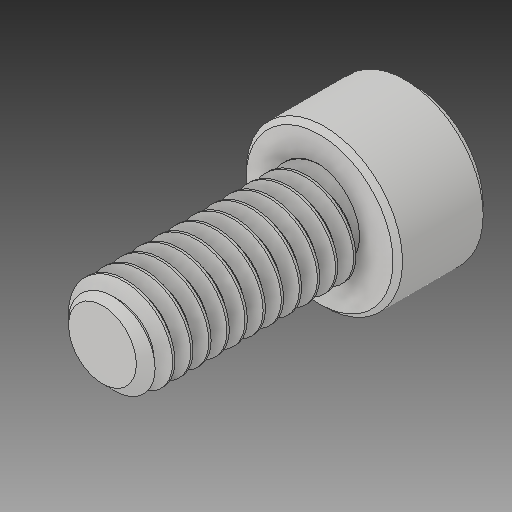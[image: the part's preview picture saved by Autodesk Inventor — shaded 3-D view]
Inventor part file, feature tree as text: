
AUTODESK INVENTOR PART (.ipt)
format: ipt  version: 2018 (Build 220112000, 112)  size: 600,576 bytes
history: native  units: in
note: dims shown in document units (in); Inventor stores cm internally (conversion verified against a paired STEP export)
features: chamfer x1
ambient origin geometry x8: Origin, YZ Plane, XZ Plane, XY Plane, X Axis, Y Axis, Z Axis, Center Point
bodies: Solid1 (feature_tree)
feature tree (1):
  chamfer  "Chamfer2"  [1 undecoded]
note: 1 required parameter value undecoded (feature->parameter linkage not recoverable at this tier; creation-order binding heuristic only, values carry confidence <= 0.55)
